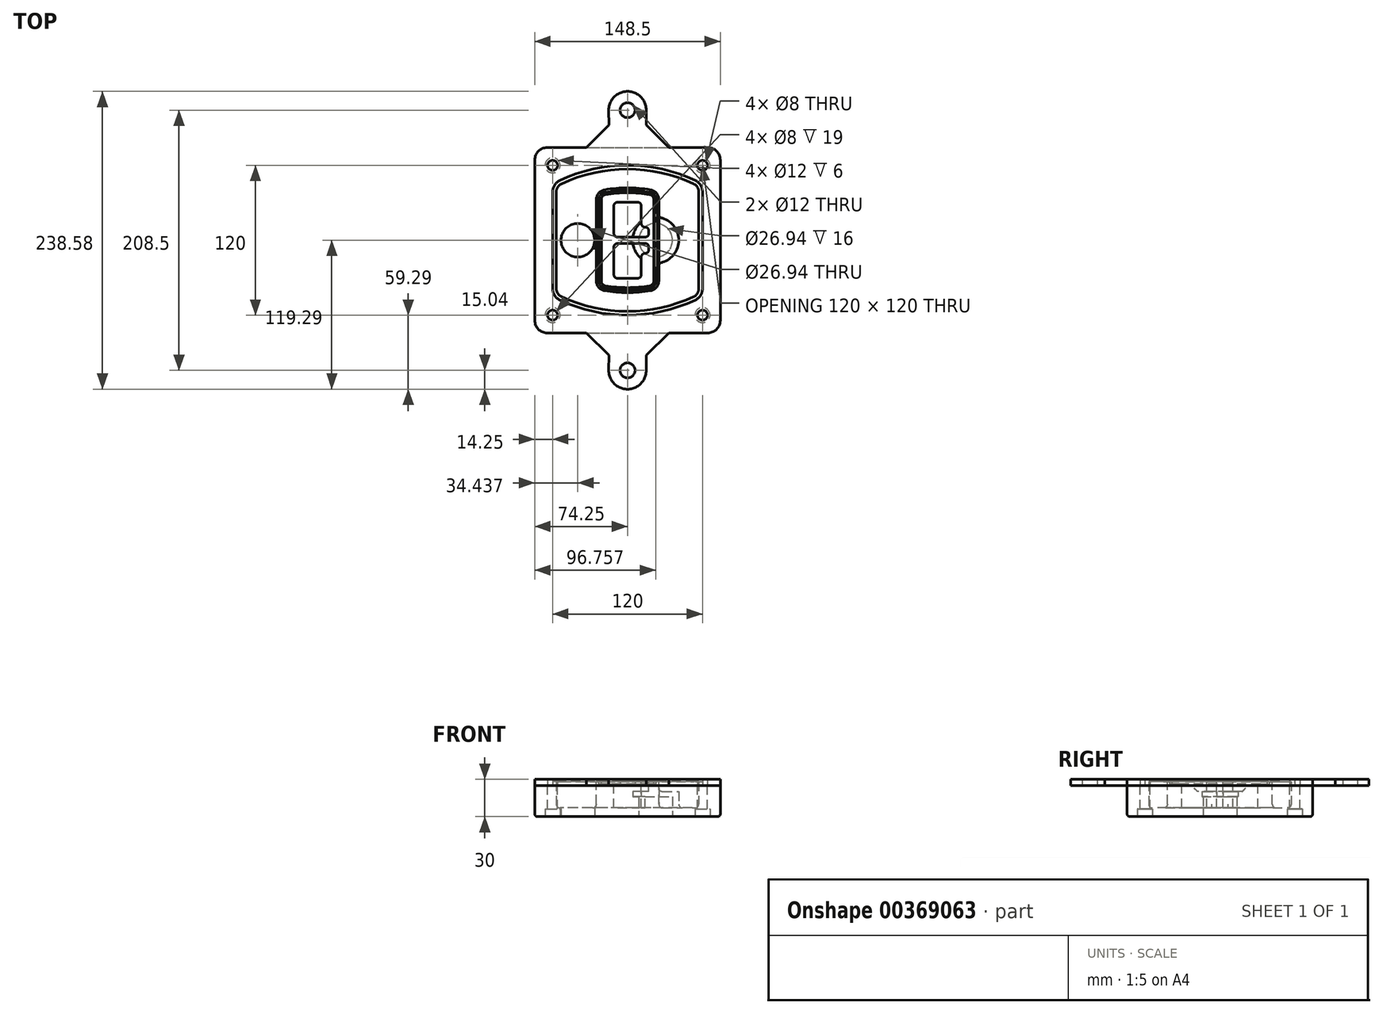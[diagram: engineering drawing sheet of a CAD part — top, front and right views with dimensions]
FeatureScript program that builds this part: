
annotation { "Feature Type Name" : "Feature", "Feature Type Description" : "" }
export const myFeature = defineFeature(function(context is Context, id is Id, definition is map)
    precondition{}
    {
        {
            var Q0;
            Q0=qCreatedBy(makeId("Top.planeOp"),FACE);
            var sketch = newSketch(context, id + "F0", { "sketchPlane" : qUnion([Q0])});
            skPoint(sketch, "E0.rect.middle", {"position": v(0, 0) * mm});
            skLineSegment(sketch, "E1.bottom", {"start": v(-64.25, -74.25) * mm, "end": v(64.25, -74.25) * mm});
            skLineSegment(sketch, "E1.top", {"start": v(-64.25, 74.25) * mm, "end": v(64.25, 74.25) * mm});
            skLineSegment(sketch, "E1.left", {"start": v(-74.25, -64.25) * mm, "end": v(-74.25, 64.25) * mm});
            skLineSegment(sketch, "E1.right", {"start": v(74.25, -64.25) * mm, "end": v(74.25, 64.25) * mm});
            skLineSegment(sketch, "E2", {"start": v(-74.25, 74.25) * mm, "end": v(74.25, -74.25) * mm, "construction": true});
            skLineSegment(sketch, "E3", {"start": v(74.25, 74.25) * mm, "end": v(-74.25, -74.25) * mm, "construction": true});
            skCircle(sketch, "E4", {"center": v(-60, 60) * mm, "radius": 4 * mm});
            skCircle(sketch, "E5", {"center": v(60, 60) * mm, "radius": 4 * mm});
            skCircle(sketch, "E6", {"center": v(60, -60) * mm, "radius": 4 * mm});
            skCircle(sketch, "E7", {"center": v(-60, -60) * mm, "radius": 4 * mm});
            skLineSegment(sketch, "E8", {"start": v(-60, 60) * mm, "end": v(60, 60) * mm, "construction": true});
            skLineSegment(sketch, "E9", {"start": v(60, 60) * mm, "end": v(60, -60) * mm, "construction": true});
            skLineSegment(sketch, "E10", {"start": v(60, -60) * mm, "end": v(-60, -60) * mm, "construction": true});
            skLineSegment(sketch, "E11", {"start": v(-60, -60) * mm, "end": v(-60, 60) * mm, "construction": true});
            skLineSegment(sketch, "E12", {"start": v(-60, 38.83) * mm, "end": v(-60, -38.83) * mm});
            skLineSegment(sketch, "E13", {"start": v(60, 38.83) * mm, "end": v(60, -38.83) * mm});
            skArc(sketch, "E14", {"start": v(54.26, 47.88) * mm, "mid": v(0, 60) * mm, "end": v(-54.26, 47.88) * mm});
            skArc(sketch, "E15", {"start": v(-54.26, -47.88) * mm, "mid": v(0, -60) * mm, "end": v(54.26, -47.88) * mm});
            skLineSegment(sketch, "E16", {"start": v(-60, 0) * mm, "end": v(60, 0) * mm, "construction": true});
            skPoint(sketch, "E17.visualSharp", {"position": v(-60, -45) * mm});
            skArc(sketch, "E17.filletArc", {"start": v(-60, -38.83) * mm, "mid": v(-58.44, -44.2) * mm, "end": v(-54.26, -47.88) * mm});
            skPoint(sketch, "E18.visualSharp", {"position": v(-60, 45) * mm});
            skArc(sketch, "E18.filletArc", {"start": v(-54.26, 47.88) * mm, "mid": v(-58.44, 44.2) * mm, "end": v(-60, 38.83) * mm});
            skPoint(sketch, "E19.visualSharp", {"position": v(60, 45) * mm});
            skArc(sketch, "E19.filletArc", {"start": v(60, 38.83) * mm, "mid": v(58.44, 44.2) * mm, "end": v(54.26, 47.88) * mm});
            skPoint(sketch, "E20.visualSharp", {"position": v(60, -45) * mm});
            skArc(sketch, "E20.filletArc", {"start": v(54.26, -47.88) * mm, "mid": v(58.44, -44.2) * mm, "end": v(60, -38.83) * mm});
            skPoint(sketch, "E21.visualSharp", {"position": v(-74.25, 74.25) * mm});
            skArc(sketch, "E21.filletArc", {"start": v(-64.25, 74.25) * mm, "mid": v(-71.32, 71.32) * mm, "end": v(-74.25, 64.25) * mm});
            skPoint(sketch, "E22.visualSharp", {"position": v(74.25, 74.25) * mm});
            skArc(sketch, "E22.filletArc", {"start": v(74.25, 64.25) * mm, "mid": v(71.32, 71.32) * mm, "end": v(64.25, 74.25) * mm});
            skPoint(sketch, "E23.visualSharp", {"position": v(74.25, -74.25) * mm});
            skArc(sketch, "E23.filletArc", {"start": v(64.25, -74.25) * mm, "mid": v(71.32, -71.32) * mm, "end": v(74.25, -64.25) * mm});
            skPoint(sketch, "E24.visualSharp", {"position": v(-74.25, -74.25) * mm});
            skArc(sketch, "E24.filletArc", {"start": v(-74.25, -64.25) * mm, "mid": v(-71.32, -71.32) * mm, "end": v(-64.25, -74.25) * mm});
            skArc(sketch, "E25.0", {"start": v(57, 38.83) * mm, "mid": v(55.9, 42.58) * mm, "end": v(52.98, 45.17) * mm});
            skLineSegment(sketch, "E25.1", {"start": v(57, 38.83) * mm, "end": v(57, -38.83) * mm});
            skArc(sketch, "E25.2", {"start": v(52.98, -45.17) * mm, "mid": v(55.9, -42.58) * mm, "end": v(57, -38.83) * mm});
            skArc(sketch, "E25.3", {"start": v(-52.98, -45.17) * mm, "mid": v(0, -57) * mm, "end": v(52.98, -45.17) * mm});
            skArc(sketch, "E25.4", {"start": v(-57, -38.83) * mm, "mid": v(-55.9, -42.58) * mm, "end": v(-52.98, -45.17) * mm});
            skArc(sketch, "E25.5", {"start": v(52.98, 45.17) * mm, "mid": v(0, 57) * mm, "end": v(-52.98, 45.17) * mm});
            skLineSegment(sketch, "E25.6", {"start": v(-57, 38.83) * mm, "end": v(-57, -38.83) * mm});
            skArc(sketch, "E25.7", {"start": v(-52.98, 45.17) * mm, "mid": v(-55.9, 42.58) * mm, "end": v(-57, 38.83) * mm});
            skArc(sketch, "E26.0", {"start": v(-55.96, 51.5) * mm, "mid": v(-61.82, 46.33) * mm, "end": v(-64, 38.83) * mm});
            skArc(sketch, "E26.1", {"start": v(55.96, 51.5) * mm, "mid": v(0, 64) * mm, "end": v(-55.96, 51.5) * mm});
            skArc(sketch, "E26.2", {"start": v(64, 38.83) * mm, "mid": v(61.82, 46.33) * mm, "end": v(55.96, 51.5) * mm});
            skLineSegment(sketch, "E26.3", {"start": v(64, 38.83) * mm, "end": v(64, -38.83) * mm});
            skArc(sketch, "E26.4", {"start": v(55.96, -51.5) * mm, "mid": v(61.82, -46.33) * mm, "end": v(64, -38.83) * mm});
            skLineSegment(sketch, "E26.5", {"start": v(-64, 38.83) * mm, "end": v(-64, -38.83) * mm});
            skArc(sketch, "E26.6", {"start": v(-55.96, -51.5) * mm, "mid": v(0, -64) * mm, "end": v(55.96, -51.5) * mm});
            skArc(sketch, "E26.7", {"start": v(-64, -38.83) * mm, "mid": v(-61.82, -46.33) * mm, "end": v(-55.96, -51.5) * mm});
            skSolve(sketch);
        }
        {
            var Q0;
            Q0=makeQuery(id+"F0.imprint","IMPRINT",FACE,{"disambiguationData":[TD([[makeQuery(id+"F0.imprint","IMPRINT",EDGE,{"derivedFrom":sQuery(id+"F0.wireOp",EDGE,"E1.bottom")}),1.0]])]});
            var Q1;
            Q1=makeQuery(id+"F0.imprint","IMPRINT",FACE,{"disambiguationData":[TD([[makeQuery(id+"F0.imprint","IMPRINT",EDGE,{"derivedFrom":sQuery(id+"F0.wireOp",EDGE,"E12")}),1.0]])]});
            var Q2;
            Q2=makeQuery(id+"F0.imprint","IMPRINT",FACE,{"disambiguationData":[TD([[makeQuery(id+"F0.imprint","IMPRINT",EDGE,{"derivedFrom":sQuery(id+"F0.wireOp",EDGE,"E25.0")}),1.0]])]});
            var Q3;
            Q3=makeQuery(id+"F0.imprint","IMPRINT",FACE,{"disambiguationData":[TD([[makeQuery(id+"F0.imprint","IMPRINT",EDGE,{"derivedFrom":sQuery(id+"F0.wireOp",EDGE,"E12")}),-1.0]])]});
            extrude(context, id + "F1", {"entities" : qUnion([Q0, Q1, Q2, Q3]), "oppositeDirection" : true, "depth" : 25 * mm});
        }
        {
            var Q0;
            Q0=makeQuery(id+"F0.imprint","IMPRINT",FACE,{"disambiguationData":[TD([[makeQuery(id+"F0.imprint","IMPRINT",EDGE,{"derivedFrom":sQuery(id+"F0.wireOp",EDGE,"E12")}),1.0]])]});
            extrude(context, id + "F2", {"entities" : qUnion([Q0]), "operationType" : NewBodyOperationType.ADD, "depth" : 3 * mm});
        }
        {
            var Q0;
            Q0=makeQuery(id+"F0.imprint","IMPRINT",FACE,{"disambiguationData":[TD([[makeQuery(id+"F0.imprint","IMPRINT",EDGE,{"derivedFrom":sQuery(id+"F0.wireOp",EDGE,"E25.0")}),1.0]])]});
            extrude(context, id + "F3", {"entities" : qUnion([Q0]), "operationType" : NewBodyOperationType.REMOVE, "oppositeDirection" : true, "depth" : 18 * mm});
        }
        {
            var Q0;
            Q0=makeQuery(id+"F2.opExtrude","CAP_FACE",FACE,{"disambiguationData":[OSD([sQuery(id+"F0.wireOp",EDGE,"E12"),sQuery(id+"F0.wireOp",EDGE,"E13"),sQuery(id+"F0.wireOp",EDGE,"E14"),sQuery(id+"F0.wireOp",EDGE,"E15"),sQuery(id+"F0.wireOp",EDGE,"E17.filletArc"),sQuery(id+"F0.wireOp",EDGE,"E18.filletArc"),sQuery(id+"F0.wireOp",EDGE,"E19.filletArc"),sQuery(id+"F0.wireOp",EDGE,"E20.filletArc"),sQuery(id+"F0.wireOp",EDGE,"E25.0"),sQuery(id+"F0.wireOp",EDGE,"E25.1"),sQuery(id+"F0.wireOp",EDGE,"E25.2"),sQuery(id+"F0.wireOp",EDGE,"E25.3"),sQuery(id+"F0.wireOp",EDGE,"E25.4"),sQuery(id+"F0.wireOp",EDGE,"E25.5"),sQuery(id+"F0.wireOp",EDGE,"E25.6"),sQuery(id+"F0.wireOp",EDGE,"E25.7")])],"isStart":false});
            var sketch = newSketch(context, id + "F4", { "sketchPlane" : qUnion([Q0])});
            skArc(sketch, "E27.0", {"start": v(-18.34, -40.45) * mm, "mid": v(0, -42) * mm, "end": v(18.34, -40.45) * mm});
            skArc(sketch, "E28.0", {"start": v(18.34, 40.45) * mm, "mid": v(0, 42) * mm, "end": v(-18.34, 40.45) * mm});
            skLineSegment(sketch, "E29", {"start": v(-25, 32.57) * mm, "end": v(-25, -32.57) * mm});
            skLineSegment(sketch, "E30", {"start": v(25, 32.57) * mm, "end": v(25, -32.57) * mm});
            skLineSegment(sketch, "E31", {"start": v(-25, 39.1) * mm, "end": v(25, 39.1) * mm, "construction": true});
            skLineSegment(sketch, "E32", {"start": v(-25, -39.1) * mm, "end": v(25, -39.1) * mm, "construction": true});
            skPoint(sketch, "E33.visualSharp", {"position": v(-25, 39.1) * mm});
            skArc(sketch, "E33.filletArc", {"start": v(-18.34, 40.45) * mm, "mid": v(-23.11, 37.73) * mm, "end": v(-25, 32.57) * mm});
            skPoint(sketch, "E34.visualSharp", {"position": v(25, 39.1) * mm});
            skArc(sketch, "E34.filletArc", {"start": v(25, 32.57) * mm, "mid": v(23.11, 37.73) * mm, "end": v(18.34, 40.45) * mm});
            skPoint(sketch, "E35.visualSharp", {"position": v(25, -39.1) * mm});
            skArc(sketch, "E35.filletArc", {"start": v(18.34, -40.45) * mm, "mid": v(23.11, -37.73) * mm, "end": v(25, -32.57) * mm});
            skPoint(sketch, "E36.visualSharp", {"position": v(-25, -39.1) * mm});
            skArc(sketch, "E36.filletArc", {"start": v(-25, -32.57) * mm, "mid": v(-23.11, -37.73) * mm, "end": v(-18.34, -40.45) * mm});
            skArc(sketch, "E37.0", {"start": v(52.98, 45.17) * mm, "mid": v(0, 57) * mm, "end": v(-52.98, 45.17) * mm});
            skArc(sketch, "E37.1", {"start": v(-52.98, 45.17) * mm, "mid": v(-55.9, 42.58) * mm, "end": v(-57, 38.83) * mm});
            skLineSegment(sketch, "E37.2", {"start": v(-57, 38.83) * mm, "end": v(-57, -38.83) * mm});
            skArc(sketch, "E37.3", {"start": v(-57, -38.83) * mm, "mid": v(-55.9, -42.58) * mm, "end": v(-52.98, -45.17) * mm});
            skArc(sketch, "E37.4", {"start": v(-52.98, -45.17) * mm, "mid": v(0, -57) * mm, "end": v(52.98, -45.17) * mm});
            skArc(sketch, "E37.5", {"start": v(52.98, -45.17) * mm, "mid": v(55.9, -42.58) * mm, "end": v(57, -38.83) * mm});
            skLineSegment(sketch, "E37.6", {"start": v(57, 38.83) * mm, "end": v(57, -38.83) * mm});
            skArc(sketch, "E37.7", {"start": v(57, 38.83) * mm, "mid": v(55.9, 42.58) * mm, "end": v(52.98, 45.17) * mm});
            skLineSegment(sketch, "E38.0", {"start": v(23, 32.57) * mm, "end": v(23, -32.57) * mm});
            skArc(sketch, "E38.1", {"start": v(18, -38.48) * mm, "mid": v(21.58, -36.44) * mm, "end": v(23, -32.57) * mm});
            skArc(sketch, "E38.2", {"start": v(-18, -38.48) * mm, "mid": v(0, -40) * mm, "end": v(18, -38.48) * mm});
            skArc(sketch, "E38.3", {"start": v(-23, -32.57) * mm, "mid": v(-21.58, -36.44) * mm, "end": v(-18, -38.48) * mm});
            skLineSegment(sketch, "E38.4", {"start": v(-23, 32.57) * mm, "end": v(-23, -32.57) * mm});
            skArc(sketch, "E38.5", {"start": v(23, 32.57) * mm, "mid": v(21.58, 36.44) * mm, "end": v(18, 38.48) * mm});
            skArc(sketch, "E38.6", {"start": v(-18, 38.48) * mm, "mid": v(-21.58, 36.44) * mm, "end": v(-23, 32.57) * mm});
            skArc(sketch, "E38.7", {"start": v(18, 38.48) * mm, "mid": v(0, 40) * mm, "end": v(-18, 38.48) * mm});
            skArc(sketch, "E39.0", {"start": v(21, 32.57) * mm, "mid": v(20.06, 35.15) * mm, "end": v(17.67, 36.5) * mm});
            skLineSegment(sketch, "E39.1", {"start": v(21, 32.57) * mm, "end": v(21, -32.57) * mm});
            skArc(sketch, "E39.2", {"start": v(17.67, -36.5) * mm, "mid": v(20.06, -35.15) * mm, "end": v(21, -32.57) * mm});
            skArc(sketch, "E39.3", {"start": v(-17.67, -36.5) * mm, "mid": v(0, -38) * mm, "end": v(17.67, -36.5) * mm});
            skArc(sketch, "E39.4", {"start": v(-21, -32.57) * mm, "mid": v(-20.06, -35.15) * mm, "end": v(-17.67, -36.5) * mm});
            skArc(sketch, "E39.5", {"start": v(17.67, 36.5) * mm, "mid": v(0, 38) * mm, "end": v(-17.67, 36.5) * mm});
            skLineSegment(sketch, "E39.6", {"start": v(-21, 32.57) * mm, "end": v(-21, -32.57) * mm});
            skArc(sketch, "E39.7", {"start": v(-17.67, 36.5) * mm, "mid": v(-20.06, 35.15) * mm, "end": v(-21, 32.57) * mm});
            skLineSegment(sketch, "E40", {"start": v(-25, 0) * mm, "end": v(25, 0) * mm, "construction": true});
            skLineSegment(sketch, "E41", {"start": v(-11, 5.5) * mm, "end": v(-11, 27.5) * mm});
            skLineSegment(sketch, "E42", {"start": v(-8, 30.5) * mm, "end": v(8, 30.5) * mm});
            skLineSegment(sketch, "E43", {"start": v(11, 27.5) * mm, "end": v(11, 13.5) * mm});
            skLineSegment(sketch, "E44", {"start": v(14, 10.5) * mm, "end": v(14, 10.5) * mm});
            skLineSegment(sketch, "E45", {"start": v(17, 7.5) * mm, "end": v(17, 5.5) * mm});
            skLineSegment(sketch, "E46", {"start": v(14, 2.5) * mm, "end": v(-8, 2.5) * mm});
            skPoint(sketch, "E47.visualSharp", {"position": v(-11, 30.5) * mm});
            skArc(sketch, "E47.filletArc", {"start": v(-8, 30.5) * mm, "mid": v(-10.12, 29.62) * mm, "end": v(-11, 27.5) * mm});
            skPoint(sketch, "E48.visualSharp", {"position": v(11, 30.5) * mm});
            skArc(sketch, "E48.filletArc", {"start": v(11, 27.5) * mm, "mid": v(10.12, 29.62) * mm, "end": v(8, 30.5) * mm});
            skPoint(sketch, "E49.visualSharp", {"position": v(11, 10.5) * mm});
            skArc(sketch, "E49.filletArc", {"start": v(11, 13.5) * mm, "mid": v(11.88, 11.38) * mm, "end": v(14, 10.5) * mm});
            skPoint(sketch, "E50.visualSharp", {"position": v(17, 10.5) * mm});
            skArc(sketch, "E50.filletArc", {"start": v(17, 7.5) * mm, "mid": v(16.12, 9.62) * mm, "end": v(14, 10.5) * mm});
            skPoint(sketch, "E51.visualSharp", {"position": v(17, 2.5) * mm});
            skArc(sketch, "E51.filletArc", {"start": v(14, 2.5) * mm, "mid": v(16.12, 3.38) * mm, "end": v(17, 5.5) * mm});
            skPoint(sketch, "E52.visualSharp", {"position": v(-11, 2.5) * mm});
            skArc(sketch, "E52.filletArc", {"start": v(-11, 5.5) * mm, "mid": v(-10.12, 3.38) * mm, "end": v(-8, 2.5) * mm});
            skLineSegment(sketch, "E53.0.MirrorCS", {"start": v(14, -2.5) * mm, "end": v(-8, -2.5) * mm});
            skArc(sketch, "E54.0.MirrorCS", {"start": v(-11, -5.5) * mm, "mid": v(-10.12, -3.38) * mm, "end": v(-8, -2.5) * mm});
            skLineSegment(sketch, "E55.0.MirrorCS", {"start": v(-11, -5.5) * mm, "end": v(-11, -27.5) * mm});
            skArc(sketch, "E56.0.MirrorCS", {"start": v(-8, -30.5) * mm, "mid": v(-10.12, -29.62) * mm, "end": v(-11, -27.5) * mm});
            skLineSegment(sketch, "E57.0.MirrorCS", {"start": v(-8, -30.5) * mm, "end": v(8, -30.5) * mm});
            skArc(sketch, "E58.0.MirrorCS", {"start": v(11, -27.5) * mm, "mid": v(10.12, -29.62) * mm, "end": v(8, -30.5) * mm});
            skLineSegment(sketch, "E59.0.MirrorCS", {"start": v(11, -27.5) * mm, "end": v(11, -13.5) * mm});
            skArc(sketch, "E60.0.MirrorCS", {"start": v(11, -13.5) * mm, "mid": v(11.88, -11.38) * mm, "end": v(14, -10.5) * mm});
            skArc(sketch, "E61.0.MirrorCS", {"start": v(17, -7.5) * mm, "mid": v(16.12, -9.62) * mm, "end": v(14, -10.5) * mm});
            skLineSegment(sketch, "E62.0.MirrorCS", {"start": v(17, -7.5) * mm, "end": v(17, -5.5) * mm});
            skArc(sketch, "E63.0.MirrorCS", {"start": v(14, -2.5) * mm, "mid": v(16.12, -3.38) * mm, "end": v(17, -5.5) * mm});
            skSolve(sketch);
        }
        {
            var Q0;
            Q0=makeQuery(id+"F4.imprint","IMPRINT",FACE,{"disambiguationData":[TD([[makeQuery(id+"F4.imprint","IMPRINT",EDGE,{"derivedFrom":sQuery(id+"F4.wireOp",EDGE,"E27.0")}),1.0]])]});
            var Q1;
            Q1=makeQuery(id+"F4.imprint","IMPRINT",FACE,{"disambiguationData":[TD([[makeQuery(id+"F4.imprint","IMPRINT",EDGE,{"derivedFrom":sQuery(id+"F4.wireOp",EDGE,"E38.0")}),-1.0]])]});
            var Q2;
            Q2=makeQuery(id+"F4.imprint","IMPRINT",FACE,{"disambiguationData":[TD([[makeQuery(id+"F4.imprint","IMPRINT",EDGE,{"derivedFrom":sQuery(id+"F4.wireOp",EDGE,"E39.0")}),1.0]])]});
            extrude(context, id + "F5", {"entities" : qUnion([Q0, Q1, Q2]), "operationType" : NewBodyOperationType.ADD, "endBound" : BoundingType.UP_TO_NEXT, "oppositeDirection" : true, "depth" : 25 * mm});
        }
        {
            var Q0;
            Q0=makeQuery(id+"F4.imprint","IMPRINT",FACE,{"disambiguationData":[TD([[makeQuery(id+"F4.imprint","IMPRINT",EDGE,{"derivedFrom":sQuery(id+"F4.wireOp",EDGE,"E38.0")}),-1.0]])]});
            extrude(context, id + "F6", {"entities" : qUnion([Q0]), "operationType" : NewBodyOperationType.REMOVE, "oppositeDirection" : true, "depth" : 2 * mm});
        }
        {
            var Q0;
            Q0=makeQuery(id+"F1.opExtrude","CAP_FACE",FACE,{"disambiguationData":[OSD([sQuery(id+"F0.wireOp",EDGE,"E1.bottom"),sQuery(id+"F0.wireOp",EDGE,"E1.top"),sQuery(id+"F0.wireOp",EDGE,"E1.left"),sQuery(id+"F0.wireOp",EDGE,"E1.right"),sQuery(id+"F0.wireOp",EDGE,"E4"),sQuery(id+"F0.wireOp",EDGE,"E5"),sQuery(id+"F0.wireOp",EDGE,"E6"),sQuery(id+"F0.wireOp",EDGE,"E7"),sQuery(id+"F0.wireOp",EDGE,"E21.filletArc"),sQuery(id+"F0.wireOp",EDGE,"E22.filletArc"),sQuery(id+"F0.wireOp",EDGE,"E23.filletArc"),sQuery(id+"F0.wireOp",EDGE,"E24.filletArc")])],"isStart":false});
            var sketch = newSketch(context, id + "F7", { "sketchPlane" : qUnion([Q0])});
            skCircle(sketch, "E64", {"center": v(22.5, 0) * mm, "radius": 13.47 * mm});
            skCircle(sketch, "E65", {"center": v(-39.81, 0) * mm, "radius": 13.47 * mm});
            skLineSegment(sketch, "E66", {"start": v(74.25, 0) * mm, "end": v(-74.25, 0) * mm});
            skCircle(sketch, "E67", {"center": v(22.5, 0) * mm, "radius": 18.47 * mm});
            skCircle(sketch, "E68", {"center": v(60, -60) * mm, "radius": 6 * mm});
            skCircle(sketch, "E69", {"center": v(-60, -60) * mm, "radius": 6 * mm});
            skCircle(sketch, "E70", {"center": v(-60, 60) * mm, "radius": 6 * mm});
            skCircle(sketch, "E71", {"center": v(60, 60) * mm, "radius": 6 * mm});
            skSolve(sketch);
        }
        {
            var Q0;
            {var subQ1=sQuery(id+"F7.wireOp",EDGE,"E66");var subQ4=sQuery(id+"F7.wireOp",EDGE,"E64");var subQ6=makeQuery(id+"F7.imprint","INTERSECT",VERTEX,{"disambiguationData":[OD(0.0)],"derivedFrom":[subQ4,subQ1]});Q0=makeQuery(id+"F7.imprint","IMPRINT",FACE,{"disambiguationData":[TD([[makeQuery(id+"F7.imprint","IMPRINT",EDGE,{"disambiguationData":[TD([[subQ6,-1.0]])],"derivedFrom":subQ4}),-1.0]])]});}
            var Q1;
            {var subQ0=sQuery(id+"F7.wireOp",EDGE,"E66");var subQ1=sQuery(id+"F7.wireOp",EDGE,"E64");var subQ3=makeQuery(id+"F7.imprint","INTERSECT",VERTEX,{"disambiguationData":[OD(0.0)],"derivedFrom":[subQ1,subQ0]});Q1=makeQuery(id+"F7.imprint","IMPRINT",FACE,{"disambiguationData":[TD([[makeQuery(id+"F7.imprint","IMPRINT",EDGE,{"disambiguationData":[TD([[subQ3,-1.0]])],"derivedFrom":subQ1}),1.0]])]});}
            var Q2;
            {var subQ0=sQuery(id+"F7.wireOp",EDGE,"E66");var subQ1=sQuery(id+"F7.wireOp",EDGE,"E64");var subQ3=makeQuery(id+"F7.imprint","INTERSECT",VERTEX,{"disambiguationData":[OD(0.0)],"derivedFrom":[subQ1,subQ0]});Q2=makeQuery(id+"F7.imprint","IMPRINT",FACE,{"disambiguationData":[TD([[makeQuery(id+"F7.imprint","IMPRINT",EDGE,{"disambiguationData":[TD([[subQ3,1.0]])],"derivedFrom":subQ1}),1.0]])]});}
            var Q3;
            {var subQ1=sQuery(id+"F7.wireOp",EDGE,"E66");var subQ4=sQuery(id+"F7.wireOp",EDGE,"E64");var subQ6=makeQuery(id+"F7.imprint","INTERSECT",VERTEX,{"disambiguationData":[OD(0.0)],"derivedFrom":[subQ4,subQ1]});Q3=makeQuery(id+"F7.imprint","IMPRINT",FACE,{"disambiguationData":[TD([[makeQuery(id+"F7.imprint","IMPRINT",EDGE,{"disambiguationData":[TD([[subQ6,1.0]])],"derivedFrom":subQ4}),-1.0]])]});}
            extrude(context, id + "F8", {"entities" : qUnion([Q0, Q1, Q2, Q3]), "operationType" : NewBodyOperationType.ADD, "oppositeDirection" : true, "depth" : 20 * mm});
        }
        {
            var Q0;
            {var subQ0=sQuery(id+"F7.wireOp",EDGE,"E66");var subQ1=sQuery(id+"F7.wireOp",EDGE,"E64");var subQ3=makeQuery(id+"F7.imprint","INTERSECT",VERTEX,{"disambiguationData":[OD(0.0)],"derivedFrom":[subQ1,subQ0]});Q0=makeQuery(id+"F7.imprint","IMPRINT",FACE,{"disambiguationData":[TD([[makeQuery(id+"F7.imprint","IMPRINT",EDGE,{"disambiguationData":[TD([[subQ3,-1.0]])],"derivedFrom":subQ1}),1.0]])]});}
            var Q1;
            {var subQ0=sQuery(id+"F7.wireOp",EDGE,"E66");var subQ1=sQuery(id+"F7.wireOp",EDGE,"E64");var subQ3=makeQuery(id+"F7.imprint","INTERSECT",VERTEX,{"disambiguationData":[OD(0.0)],"derivedFrom":[subQ1,subQ0]});Q1=makeQuery(id+"F7.imprint","IMPRINT",FACE,{"disambiguationData":[TD([[makeQuery(id+"F7.imprint","IMPRINT",EDGE,{"disambiguationData":[TD([[subQ3,1.0]])],"derivedFrom":subQ1}),1.0]])]});}
            extrude(context, id + "F9", {"entities" : qUnion([Q0, Q1]), "operationType" : NewBodyOperationType.REMOVE, "oppositeDirection" : true, "depth" : 16 * mm});
        }
        {
            var Q0;
            {var subQ0=sQuery(id+"F7.wireOp",EDGE,"E66");var subQ1=sQuery(id+"F7.wireOp",EDGE,"E65");var subQ3=makeQuery(id+"F7.imprint","INTERSECT",VERTEX,{"disambiguationData":[OD(0.0)],"derivedFrom":[subQ1,subQ0]});Q0=makeQuery(id+"F7.imprint","IMPRINT",FACE,{"disambiguationData":[TD([[makeQuery(id+"F7.imprint","IMPRINT",EDGE,{"disambiguationData":[TD([[subQ3,-1.0]])],"derivedFrom":subQ1}),1.0]])]});}
            var Q1;
            {var subQ0=sQuery(id+"F7.wireOp",EDGE,"E66");var subQ1=sQuery(id+"F7.wireOp",EDGE,"E65");var subQ3=makeQuery(id+"F7.imprint","INTERSECT",VERTEX,{"disambiguationData":[OD(0.0)],"derivedFrom":[subQ1,subQ0]});Q1=makeQuery(id+"F7.imprint","IMPRINT",FACE,{"disambiguationData":[TD([[makeQuery(id+"F7.imprint","IMPRINT",EDGE,{"disambiguationData":[TD([[subQ3,1.0]])],"derivedFrom":subQ1}),1.0]])]});}
            extrude(context, id + "F10", {"entities" : qUnion([Q0, Q1]), "operationType" : NewBodyOperationType.REMOVE, "oppositeDirection" : true, "depth" : 25 * mm});
        }
        {
            var Q0;
            Q0=makeQuery(id+"F7.imprint","IMPRINT",FACE,{"disambiguationData":[TD([[makeQuery(id+"F7.imprint","IMPRINT",EDGE,{"derivedFrom":sQuery(id+"F7.wireOp",EDGE,"E68")}),1.0]])]});
            var Q1;
            Q1=makeQuery(id+"F7.imprint","IMPRINT",FACE,{"disambiguationData":[TD([[makeQuery(id+"F7.imprint","IMPRINT",EDGE,{"derivedFrom":makeQuery(id+"F1.opExtrude","CAP_EDGE",EDGE,{"disambiguationData":[OSD([sQuery(id+"F0.wireOp",EDGE,"E5")])],"isStart":false})}),-1.0]])]});
            var Q2;
            Q2=makeQuery(id+"F7.imprint","IMPRINT",FACE,{"disambiguationData":[TD([[makeQuery(id+"F7.imprint","IMPRINT",EDGE,{"derivedFrom":sQuery(id+"F7.wireOp",EDGE,"E69")}),1.0]])]});
            var Q3;
            Q3=makeQuery(id+"F7.imprint","IMPRINT",FACE,{"disambiguationData":[TD([[makeQuery(id+"F7.imprint","IMPRINT",EDGE,{"derivedFrom":makeQuery(id+"F1.opExtrude","CAP_EDGE",EDGE,{"disambiguationData":[OSD([sQuery(id+"F0.wireOp",EDGE,"E4")])],"isStart":false})}),-1.0]])]});
            var Q4;
            Q4=makeQuery(id+"F7.imprint","IMPRINT",FACE,{"disambiguationData":[TD([[makeQuery(id+"F7.imprint","IMPRINT",EDGE,{"derivedFrom":sQuery(id+"F7.wireOp",EDGE,"E70")}),1.0]])]});
            var Q5;
            Q5=makeQuery(id+"F7.imprint","IMPRINT",FACE,{"disambiguationData":[TD([[makeQuery(id+"F7.imprint","IMPRINT",EDGE,{"derivedFrom":makeQuery(id+"F1.opExtrude","CAP_EDGE",EDGE,{"disambiguationData":[OSD([sQuery(id+"F0.wireOp",EDGE,"E7")])],"isStart":false})}),-1.0]])]});
            var Q6;
            Q6=makeQuery(id+"F7.imprint","IMPRINT",FACE,{"disambiguationData":[TD([[makeQuery(id+"F7.imprint","IMPRINT",EDGE,{"derivedFrom":sQuery(id+"F7.wireOp",EDGE,"E71")}),1.0]])]});
            var Q7;
            Q7=makeQuery(id+"F7.imprint","IMPRINT",FACE,{"disambiguationData":[TD([[makeQuery(id+"F7.imprint","IMPRINT",EDGE,{"derivedFrom":makeQuery(id+"F1.opExtrude","CAP_EDGE",EDGE,{"disambiguationData":[OSD([sQuery(id+"F0.wireOp",EDGE,"E6")])],"isStart":false})}),-1.0]])]});
            extrude(context, id + "F11", {"entities" : qUnion([Q0, Q1, Q2, Q3, Q4, Q5, Q6, Q7]), "operationType" : NewBodyOperationType.REMOVE, "oppositeDirection" : true, "depth" : 6 * mm});
        }
        {
            var Q0;
            Q0=makeQuery(id+"F9.boolean.opBoolean","COPY",FACE,{"derivedFrom":makeQuery(id+"F9.opExtrude","CAP_FACE",FACE,{"disambiguationData":[OSD([sQuery(id+"F7.wireOp",EDGE,"E64")])],"isStart":false})});
            var sketch = newSketch(context, id + "F12", { "sketchPlane" : qUnion([Q0])});
            skArc(sketch, "E72.0", {"start": v(11, 14.45) * mm, "mid": v(6.45, 9.13) * mm, "end": v(4.2, 2.5) * mm});
            skArc(sketch, "E72.1", {"start": v(4.2, -2.5) * mm, "mid": v(6.45, -9.13) * mm, "end": v(11, -14.45) * mm});
            skLineSegment(sketch, "E73", {"start": v(4.2, -2.5) * mm, "end": v(14, -2.5) * mm});
            skLineSegment(sketch, "E74.0", {"start": v(14, 2.5) * mm, "end": v(4.2, 2.5) * mm});
            skArc(sketch, "E74.1", {"start": v(14, 2.5) * mm, "mid": v(16.12, 3.38) * mm, "end": v(17, 5.5) * mm});
            skLineSegment(sketch, "E74.2", {"start": v(17, 7.5) * mm, "end": v(17, 5.5) * mm});
            skArc(sketch, "E74.3", {"start": v(17, 7.5) * mm, "mid": v(16.12, 9.62) * mm, "end": v(14, 10.5) * mm});
            skArc(sketch, "E74.4", {"start": v(11, 13.5) * mm, "mid": v(11.88, 11.38) * mm, "end": v(14, 10.5) * mm});
            skLineSegment(sketch, "E74.5", {"start": v(11, 14.45) * mm, "end": v(11, 13.5) * mm});
            skLineSegment(sketch, "E74.7", {"start": v(14, -2.5) * mm, "end": v(4.2, -2.5) * mm});
            skArc(sketch, "E74.8", {"start": v(14, -2.5) * mm, "mid": v(16.12, -3.38) * mm, "end": v(17, -5.5) * mm});
            skLineSegment(sketch, "E74.9", {"start": v(17, -7.5) * mm, "end": v(17, -5.5) * mm});
            skArc(sketch, "E74.10", {"start": v(17, -7.5) * mm, "mid": v(16.12, -9.62) * mm, "end": v(14, -10.5) * mm});
            skArc(sketch, "E74.11", {"start": v(11, -13.5) * mm, "mid": v(11.88, -11.38) * mm, "end": v(14, -10.5) * mm});
            skLineSegment(sketch, "E74.12", {"start": v(11, -14.45) * mm, "end": v(11, -13.5) * mm});
            skPoint(sketch, "E75.orphan", {"position": v(11, -27.5) * mm});
            skPoint(sketch, "E76.orphan", {"position": v(-8, -2.5) * mm});
            skPoint(sketch, "E77.orphan", {"position": v(-8, 2.5) * mm});
            skPoint(sketch, "E78.orphan", {"position": v(11, 27.5) * mm});
            skSolve(sketch);
        }
        {
            var Q0;
            {var subQ7=sQuery(id+"F12.wireOp",EDGE,"E72.0");var subQ14=sQuery(id+"F12.wireOp",EDGE,"E72.1");var subQ16=sQuery(id+"F12.wireOp",EDGE,"E74.1");var subQ18=sQuery(id+"F12.wireOp",EDGE,"E74.8");Q0=qUnion([makeQuery(id+"F12.imprint","IMPRINT",FACE,{"disambiguationData":[TD([[makeQuery(id+"F12.imprint","IMPRINT",EDGE,{"derivedFrom":subQ7}),1.0]])]}),makeQuery(id+"F12.imprint","IMPRINT",FACE,{"disambiguationData":[TD([[makeQuery(id+"F12.imprint","IMPRINT",EDGE,{"derivedFrom":subQ14}),1.0]])]}),makeQuery(id+"F12.imprint","IMPRINT",FACE,{"disambiguationData":[TD([[makeQuery(id+"F12.imprint","IMPRINT",EDGE,{"derivedFrom":subQ16}),1.0]])]}),makeQuery(id+"F12.imprint","IMPRINT",FACE,{"disambiguationData":[TD([[makeQuery(id+"F12.imprint","IMPRINT",EDGE,{"derivedFrom":subQ18}),-1.0]])]})]);}
            var Q1;
            Q1=makeQuery(id+"F5.boolean.opBoolean","SPLIT",FACE,{"disambiguationData":[TD([makeQuery(id+"F5.opExtrude","SWEPT_FACE",FACE,{"disambiguationData":[OSD([sQuery(id+"F4.wireOp",EDGE,"E41")])]})])],"derivedFrom":makeQuery(id+"F3.boolean.opBoolean","COPY",FACE,{"derivedFrom":makeQuery(id+"F3.opExtrude","CAP_FACE",FACE,{"disambiguationData":[OSD([sQuery(id+"F0.wireOp",EDGE,"E25.0"),sQuery(id+"F0.wireOp",EDGE,"E25.1"),sQuery(id+"F0.wireOp",EDGE,"E25.2"),sQuery(id+"F0.wireOp",EDGE,"E25.3"),sQuery(id+"F0.wireOp",EDGE,"E25.4"),sQuery(id+"F0.wireOp",EDGE,"E25.5"),sQuery(id+"F0.wireOp",EDGE,"E25.6"),sQuery(id+"F0.wireOp",EDGE,"E25.7")])],"isStart":false})})});
            extrude(context, id + "F13", {"entities" : qUnion([Q0]), "operationType" : NewBodyOperationType.REMOVE, "endBound" : BoundingType.UP_TO_SURFACE, "endBoundEntityFace" : qUnion([Q1]), "depth" : 25 * mm});
        }
        {
            var Q0;
            Q0=makeQuery(id+"F3.boolean.opBoolean","COPY",EDGE,{"derivedFrom":makeQuery(id+"F3.opExtrude","CAP_EDGE",EDGE,{"disambiguationData":[OSD([sQuery(id+"F0.wireOp",EDGE,"E25.6")])],"isStart":false})});
            var Q1;
            Q1=makeQuery(id+"F8.boolean.opBoolean","INTERSECT",EDGE,{"derivedFrom":[makeQuery(id+"F5.opExtrude","SWEPT_FACE",FACE,{"disambiguationData":[OSD([sQuery(id+"F4.wireOp",EDGE,"E30")])]}),makeQuery(id+"F8.opExtrude","CAP_FACE",FACE,{"disambiguationData":[OSD([sQuery(id+"F7.wireOp",EDGE,"E67")])],"isStart":false})]});
            var Q2;
            Q2=makeQuery(id+"F8.boolean.opBoolean","INTERSECT",EDGE,{"disambiguationData":[OD(1.0)],"derivedFrom":[makeQuery(id+"F5.opExtrude","SWEPT_FACE",FACE,{"disambiguationData":[OSD([sQuery(id+"F4.wireOp",EDGE,"E30")])]}),makeQuery(id+"F8.opExtrude","SWEPT_FACE",FACE,{"disambiguationData":[OSD([sQuery(id+"F7.wireOp",EDGE,"E67")])]})]});
            var Q3;
            {var subQ0=sQuery(id+"F4.wireOp",EDGE,"E30");Q3=makeQuery(id+"F8.boolean.opBoolean","SPLIT",EDGE,{"disambiguationData":[TD([makeQuery(id+"F5.opExtrude","SWEPT_FACE",FACE,{"disambiguationData":[OSD([sQuery(id+"F4.wireOp",EDGE,"E35.filletArc")])]})])],"derivedFrom":makeQuery(id+"F5.opExtrude","CAP_EDGE",EDGE,{"disambiguationData":[OSD([subQ0])],"isStart":false})});}
            var Q4;
            {var subQ0=sQuery(id+"F0.wireOp",EDGE,"E25.7");var subQ1=sQuery(id+"F0.wireOp",EDGE,"E25.1");var subQ2=sQuery(id+"F0.wireOp",EDGE,"E25.6");var subQ3=sQuery(id+"F0.wireOp",EDGE,"E25.5");var subQ4=sQuery(id+"F0.wireOp",EDGE,"E25.4");var subQ5=sQuery(id+"F0.wireOp",EDGE,"E25.0");var subQ6=sQuery(id+"F0.wireOp",EDGE,"E25.2");var subQ7=sQuery(id+"F0.wireOp",EDGE,"E25.3");Q4=makeQuery(id+"F8.boolean.opBoolean","INTERSECT",EDGE,{"derivedFrom":[makeQuery(id+"F5.boolean.opBoolean","SPLIT",FACE,{"disambiguationData":[TD([makeQuery(id+"F2.opExtrude","SWEPT_FACE",FACE,{"disambiguationData":[OSD([subQ5])]})])],"derivedFrom":makeQuery(id+"F3.boolean.opBoolean","COPY",FACE,{"derivedFrom":makeQuery(id+"F3.opExtrude","CAP_FACE",FACE,{"disambiguationData":[OSD([subQ5,subQ1,subQ6,subQ7,subQ4,subQ3,subQ2,subQ0])],"isStart":false})})}),makeQuery(id+"F8.opExtrude","SWEPT_FACE",FACE,{"disambiguationData":[OSD([sQuery(id+"F7.wireOp",EDGE,"E67")])]})]});}
            var Q5;
            Q5=makeQuery(id+"F8.boolean.opBoolean","INTERSECT",EDGE,{"disambiguationData":[OD(0.0)],"derivedFrom":[makeQuery(id+"F5.opExtrude","SWEPT_FACE",FACE,{"disambiguationData":[OSD([sQuery(id+"F4.wireOp",EDGE,"E30")])]}),makeQuery(id+"F8.opExtrude","SWEPT_FACE",FACE,{"disambiguationData":[OSD([sQuery(id+"F7.wireOp",EDGE,"E67")])]})]});
            fillet(context, id + "F14", {"entities" : qUnion([Q0, Q1, Q2, Q3, Q4, Q5]), "radius" : 3 * mm, "tangentPropagation" : true, "allowEdgeOverflow" : false});
        }
        {
            var Q0;
            Q0=makeQuery(id+"F1.opExtrude","CAP_EDGE",EDGE,{"disambiguationData":[OSD([sQuery(id+"F0.wireOp",EDGE,"E1.bottom")])],"isStart":false});
            fillet(context, id + "F15", {"entities" : qUnion([Q0]), "radius" : 2 * mm, "tangentPropagation" : true, "allowEdgeOverflow" : false});
        }
        {
            var Q0;
            {var subQ0=sQuery(id+"F0.wireOp",EDGE,"E21.filletArc");var subQ1=sQuery(id+"F0.wireOp",EDGE,"E7");var subQ2=sQuery(id+"F0.wireOp",EDGE,"E6");var subQ3=sQuery(id+"F0.wireOp",EDGE,"E5");var subQ4=sQuery(id+"F0.wireOp",EDGE,"E4");var subQ5=sQuery(id+"F0.wireOp",EDGE,"E22.filletArc");var subQ6=sQuery(id+"F0.wireOp",EDGE,"E1.bottom");var subQ7=sQuery(id+"F0.wireOp",EDGE,"E1.right");var subQ8=sQuery(id+"F0.wireOp",EDGE,"E1.top");var subQ9=sQuery(id+"F0.wireOp",EDGE,"E1.left");var subQ10=sQuery(id+"F0.wireOp",EDGE,"E23.filletArc");var subQ11=sQuery(id+"F0.wireOp",EDGE,"E24.filletArc");Q0=makeQuery(id+"F2.boolean.opBoolean","SPLIT",FACE,{"disambiguationData":[TD([makeQuery(id+"F1.opExtrude","SWEPT_FACE",FACE,{"disambiguationData":[OSD([subQ6])]})])],"derivedFrom":makeQuery(id+"F1.opExtrude","CAP_FACE",FACE,{"disambiguationData":[OSD([subQ6,subQ8,subQ9,subQ7,subQ4,subQ3,subQ2,subQ1,subQ0,subQ5,subQ10,subQ11])],"isStart":true})});}
            var sketch = newSketch(context, id + "F16", { "sketchPlane" : qUnion([Q0])});
            skCircle(sketch, "E79", {"center": v(0, 104.25) * mm, "radius": 6 * mm});
            skArc(sketch, "E80", {"start": v(14.98, 104.25) * mm, "mid": v(-0.02, 119.3) * mm, "end": v(-15.02, 104.25) * mm});
            skLineSegment(sketch, "E81", {"start": v(-15.02, 104.25) * mm, "end": v(-15, 92.25) * mm});
            skLineSegment(sketch, "E82", {"start": v(14.98, 104.25) * mm, "end": v(14.94, 92.25) * mm});
            skLineSegment(sketch, "E83", {"start": v(-15, 92.25) * mm, "end": v(-33, 74.25) * mm});
            skLineSegment(sketch, "E84", {"start": v(14.94, 92.25) * mm, "end": v(32.94, 74.25) * mm});
            skLineSegment(sketch, "E85", {"start": v(0, 104.25) * mm, "end": v(0, 74.25) * mm, "construction": true});
            skLineSegment(sketch, "E86", {"start": v(-74.25, 0) * mm, "end": v(74.25, 0) * mm, "construction": true});
            skLineSegment(sketch, "E87.MirrorCS", {"start": v(14.98, -104.25) * mm, "end": v(14.94, -92.25) * mm});
            skLineSegment(sketch, "E88.MirrorCS", {"start": v(14.94, -92.25) * mm, "end": v(32.94, -74.25) * mm});
            skLineSegment(sketch, "E89.MirrorCS", {"start": v(-15, -92.25) * mm, "end": v(-33, -74.25) * mm});
            skLineSegment(sketch, "E90.MirrorCS", {"start": v(-15.02, -104.25) * mm, "end": v(-15, -92.25) * mm});
            skLineSegment(sketch, "E91.MirrorCS", {"start": v(0, -104.25) * mm, "end": v(0, -74.25) * mm, "construction": true});
            skCircle(sketch, "E92.MirrorC", {"center": v(0, -104.25) * mm, "radius": 6 * mm});
            skArc(sketch, "E93.MirrorCS", {"start": v(14.98, -104.25) * mm, "mid": v(-0.02, -119.3) * mm, "end": v(-15.02, -104.25) * mm});
            skSolve(sketch);
        }
        {
            var Q0;
            Q0=makeQuery(id+"F16.imprint","IMPRINT",FACE,{"disambiguationData":[TD([[makeQuery(id+"F16.imprint","IMPRINT",EDGE,{"derivedFrom":sQuery(id+"F16.wireOp",EDGE,"E79")}),-1.0]])]});
            var Q1;
            Q1=makeQuery(id+"F16.imprint","IMPRINT",FACE,{"disambiguationData":[TD([[makeQuery(id+"F16.imprint","IMPRINT",EDGE,{"derivedFrom":sQuery(id+"F16.wireOp",EDGE,"E87.MirrorCS")}),1.0]])]});
            var Q2;
            Q2=makeQuery(id+"F16.imprint","IMPRINT",FACE,{"disambiguationData":[TD([[makeQuery(id+"F16.imprint","IMPRINT",EDGE,{"derivedFrom":makeQuery(id+"F1.opExtrude","CAP_EDGE",EDGE,{"disambiguationData":[OSD([sQuery(id+"F0.wireOp",EDGE,"E1.left")])],"isStart":true})}),-1.0]])]});
            extrude(context, id + "F17", {"entities" : qUnion([Q0, Q1, Q2]), "depth" : 5 * mm});
        }
    });
